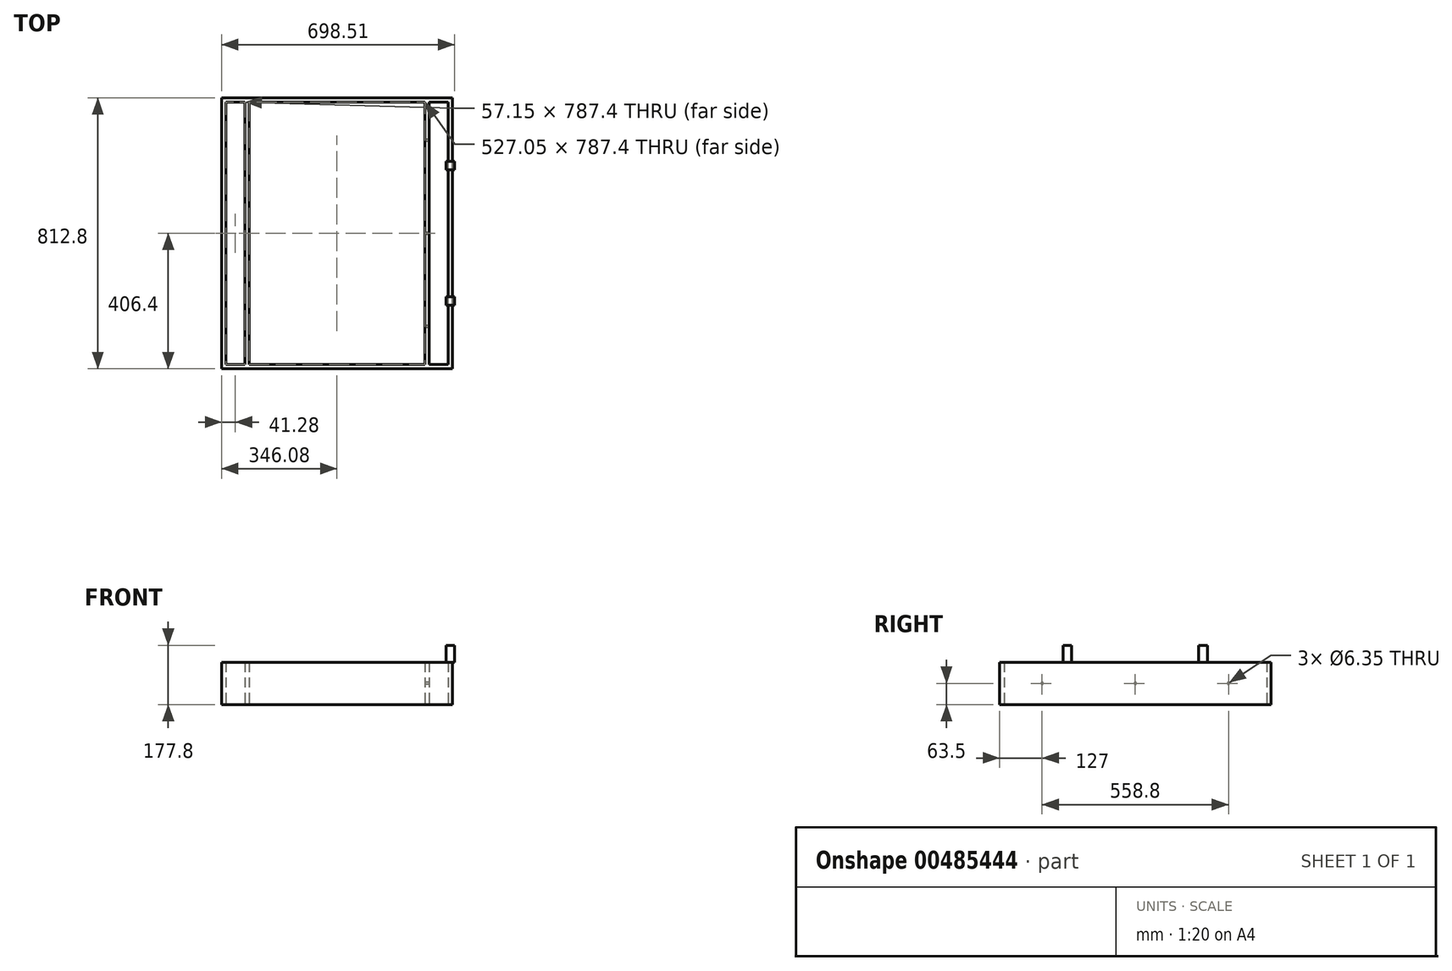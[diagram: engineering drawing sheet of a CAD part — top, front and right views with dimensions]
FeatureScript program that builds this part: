
annotation { "Feature Type Name" : "Feature", "Feature Type Description" : "" }
export const myFeature = defineFeature(function(context is Context, id is Id, definition is map)
    precondition{}
    {
        {
            var Q0;
            Q0=qCreatedBy(makeId("Top.planeOp"),FACE);
            var sketch = newSketch(context, id + "F0", { "sketchPlane" : qUnion([Q0])});
            skLineSegment(sketch, "E0.bottom", {"start": v(346.08, -406.4) * mm, "end": v(-346.08, -406.4) * mm});
            skLineSegment(sketch, "E0.top", {"start": v(346.08, 406.4) * mm, "end": v(-346.07, 406.4) * mm});
            skLineSegment(sketch, "E0.left", {"start": v(346.08, -406.4) * mm, "end": v(346.08, 406.4) * mm});
            skLineSegment(sketch, "E0.right", {"start": v(-346.07, -406.4) * mm, "end": v(-346.07, 406.4) * mm});
            skPoint(sketch, "E0.middle", {"position": v(0, 0) * mm});
            skLineSegment(sketch, "E1", {"start": v(-346.07, 406.4) * mm, "end": v(-290.29, 406.4) * mm});
            skLineSegment(sketch, "E2", {"start": v(-290.29, 406.4) * mm, "end": v(-294.23, 406.4) * mm});
            skLineSegment(sketch, "E3", {"start": v(-294.23, 406.4) * mm, "end": v(-346.07, 406.4) * mm});
            skLineSegment(sketch, "E4", {"start": v(-276.22, 383.12) * mm, "end": v(-276.22, 393.7) * mm});
            skLineSegment(sketch, "E5", {"start": v(-263.52, 383.12) * mm, "end": v(-263.52, 393.7) * mm});
            skLineSegment(sketch, "E6", {"start": v(-333.38, -393.7) * mm, "end": v(-333.38, 393.7) * mm});
            skLineSegment(sketch, "E7", {"start": v(-333.37, -393.7) * mm, "end": v(-333.37, -393.7) * mm});
            skLineSegment(sketch, "E8", {"start": v(-276.22, 383.12) * mm, "end": v(-276.23, -393.7) * mm});
            skLineSegment(sketch, "E9", {"start": v(-263.52, 383.12) * mm, "end": v(-263.53, -393.7) * mm});
            skLineSegment(sketch, "E10.MirrorCS", {"start": v(333.38, -393.7) * mm, "end": v(333.38, 393.7) * mm});
            skLineSegment(sketch, "E11.MirrorCS", {"start": v(276.22, 383.12) * mm, "end": v(276.22, 393.7) * mm});
            skLineSegment(sketch, "E12.MirrorCS", {"start": v(276.23, 383.12) * mm, "end": v(276.23, -393.7) * mm});
            skLineSegment(sketch, "E13.MirrorCS", {"start": v(263.52, 383.12) * mm, "end": v(263.52, 393.7) * mm});
            skLineSegment(sketch, "E14.MirrorCS", {"start": v(263.52, 383.12) * mm, "end": v(263.52, -393.7) * mm});
            skLineSegment(sketch, "E15", {"start": v(-346.07, 406.4) * mm, "end": v(-346.07, 393.7) * mm});
            skPoint(sketch, "E16.endSnap0", {"position": v(-346.07, 400.05) * mm});
            skLineSegment(sketch, "E17", {"start": v(-333.38, 393.7) * mm, "end": v(-276.22, 393.7) * mm});
            skLineSegment(sketch, "E18", {"start": v(346.08, -406.4) * mm, "end": v(346.08, -393.7) * mm});
            skLineSegment(sketch, "E19", {"start": v(333.38, -393.7) * mm, "end": v(276.23, -393.7) * mm});
            skPoint(sketch, "E20.orphan", {"position": v(-333.37, -406.4) * mm});
            skPoint(sketch, "E21.orphan", {"position": v(-276.23, -406.4) * mm});
            skLineSegment(sketch, "E22.trimOffspring", {"start": v(-276.23, -393.7) * mm, "end": v(-333.37, -393.7) * mm});
            skPoint(sketch, "E23.orphan", {"position": v(-263.53, -406.4) * mm});
            skPoint(sketch, "E24.MirrorCS.start.orphan", {"position": v(-333.37, -393.7) * mm});
            skLineSegment(sketch, "E25.trimOffspring", {"start": v(-263.52, 393.7) * mm, "end": v(263.52, 393.7) * mm});
            skPoint(sketch, "E26.orphan", {"position": v(-263.52, 406.4) * mm});
            skPoint(sketch, "E27.orphan", {"position": v(-276.22, 406.4) * mm});
            skPoint(sketch, "E28.orphan", {"position": v(-333.38, 406.4) * mm});
            skPoint(sketch, "E29.orphan", {"position": v(263.52, 406.4) * mm});
            skPoint(sketch, "E30.orphan", {"position": v(276.22, 406.4) * mm});
            skPoint(sketch, "E31.orphan", {"position": v(333.38, 406.4) * mm});
            skPoint(sketch, "E32.orphan", {"position": v(276.23, -406.4) * mm});
            skLineSegment(sketch, "E33.trimOffspring", {"start": v(263.53, -393.7) * mm, "end": v(-263.53, -393.7) * mm});
            skPoint(sketch, "E34.orphan", {"position": v(263.53, -406.4) * mm});
            skPoint(sketch, "E35.MirrorCS.end.orphan", {"position": v(333.37, -406.4) * mm});
            skPoint(sketch, "E35.MirrorCS.start.orphan", {"position": v(333.37, -393.7) * mm});
            skLineSegment(sketch, "E36.trimOffspring", {"start": v(276.22, 393.7) * mm, "end": v(333.38, 393.7) * mm});
            skSolve(sketch);
        }
        {
            var Q0;
            Q0 = qSketchRegion(id + "F0", true);
            extrude(context, id + "F1", {"entities" : qUnion([Q0]), "endBound" : BoundingType.SYMMETRIC, "depth" : 127 * mm});
        }
        {
            var Q0;
            Q0=makeQuery(id+"F1.opExtrude","SWEPT_FACE",FACE,{"disambiguationData":[OSD([sQuery(id+"F0.wireOp",EDGE,"E13.MirrorCS"),sQuery(id+"F0.wireOp",EDGE,"E14.MirrorCS")])]});
            var sketch = newSketch(context, id + "F2", { "sketchPlane" : qUnion([Q0])});
            skCircle(sketch, "E37", {"center": v(0, 0) * mm, "radius": 3.18 * mm});
            skCircle(sketch, "E38", {"center": v(-279.4, 0) * mm, "radius": 3.18 * mm});
            skCircle(sketch, "E39", {"center": v(279.4, 0) * mm, "radius": 3.18 * mm});
            skSolve(sketch);
        }
        {
            var Q0;
            Q0 = qSketchRegion(id + "F2", true);
            extrude(context, id + "F3", {"entities" : qUnion([Q0]), "operationType" : NewBodyOperationType.REMOVE, "oppositeDirection" : true, "depth" : 12.7 * mm});
        }
        {
            var Q0;
            Q0=makeQuery(id+"F1.opExtrude","SWEPT_FACE",FACE,{"disambiguationData":[OSD([sQuery(id+"F0.wireOp",EDGE,"E0.left"),sQuery(id+"F0.wireOp",EDGE,"E18")])]});
            var Q1;
            Q1=makeQuery(id+"F1.opExtrude","SWEPT_FACE",FACE,{"disambiguationData":[OSD([sQuery(id+"F0.wireOp",EDGE,"E10.MirrorCS")])]});
            cPlane(context, id + "F4", {"entities" : qUnion([Q0, Q1]), "cplaneType" : CPlaneType.MID_PLANE, "offset" : 25.4 * mm, "width" : 152.4 * mm, "height" : 152.4 * mm});
        }
        {
            var Q0;
            Q0=qCreatedBy(id+"F4.planeOp",FACE);
            var sketch = newSketch(context, id + "F5", { "sketchPlane" : qUnion([Q0])});
            skLineSegment(sketch, "E40", {"start": v(-203.2, 63.5) * mm, "end": v(-215.9, 63.5) * mm});
            skLineSegment(sketch, "E41", {"start": v(-203.2, 63.5) * mm, "end": v(-190.5, 63.5) * mm});
            skLineSegment(sketch, "E42", {"start": v(-215.9, 63.5) * mm, "end": v(-215.9, 114.3) * mm});
            skLineSegment(sketch, "E43", {"start": v(-190.5, 63.5) * mm, "end": v(-190.5, 114.3) * mm});
            skLineSegment(sketch, "E44", {"start": v(-215.9, 114.3) * mm, "end": v(-190.5, 114.3) * mm});
            skLineSegment(sketch, "E45.MirrorCS", {"start": v(203.2, 63.5) * mm, "end": v(190.5, 63.5) * mm});
            skLineSegment(sketch, "E46.MirrorCS", {"start": v(203.2, 63.5) * mm, "end": v(215.9, 63.5) * mm});
            skLineSegment(sketch, "E47.MirrorCS", {"start": v(215.9, 114.3) * mm, "end": v(190.5, 114.3) * mm});
            skLineSegment(sketch, "E48.MirrorCS", {"start": v(215.9, 63.5) * mm, "end": v(215.9, 114.3) * mm});
            skLineSegment(sketch, "E49.MirrorCS", {"start": v(190.5, 63.5) * mm, "end": v(190.5, 114.3) * mm});
            skSolve(sketch);
        }
        {
            var Q0;
            Q0 = qSketchRegion(id + "F5", true);
            extrude(context, id + "F6", {"entities" : qUnion([Q0]), "operationType" : NewBodyOperationType.ADD, "endBound" : BoundingType.SYMMETRIC, "depth" : 25.4 * mm});
        }
        {
            var Q0;
            Q0=makeQuery(id+"F1.opExtrude","SWEPT_FACE",FACE,{"disambiguationData":[OSD([sQuery(id+"F0.wireOp",EDGE,"E11.MirrorCS"),sQuery(id+"F0.wireOp",EDGE,"E12.MirrorCS")])]});
            var Q1;
            Q1=makeQuery(id+"F1.opExtrude","SWEPT_FACE",FACE,{"disambiguationData":[OSD([sQuery(id+"F0.wireOp",EDGE,"E10.MirrorCS")])]});
            cPlane(context, id + "F7", {"entities" : qUnion([Q0, Q1]), "cplaneType" : CPlaneType.MID_PLANE, "offset" : 25.4 * mm, "width" : 152.4 * mm, "height" : 152.4 * mm});
        }
        {
            var Q0;
            Q0=makeQuery(id+"F1.opExtrude","SWEPT_FACE",FACE,{"disambiguationData":[OSD([sQuery(id+"F0.wireOp",EDGE,"E5"),sQuery(id+"F0.wireOp",EDGE,"E9")])]});
            var Q1;
            Q1=makeQuery(id+"F1.opExtrude","SWEPT_FACE",FACE,{"disambiguationData":[OSD([sQuery(id+"F0.wireOp",EDGE,"E10.MirrorCS")])]});
            cPlane(context, id + "F8", {"entities" : qUnion([Q0, Q1]), "cplaneType" : CPlaneType.MID_PLANE, "offset" : 25.4 * mm, "width" : 152.4 * mm, "height" : 152.4 * mm});
        }
    });
